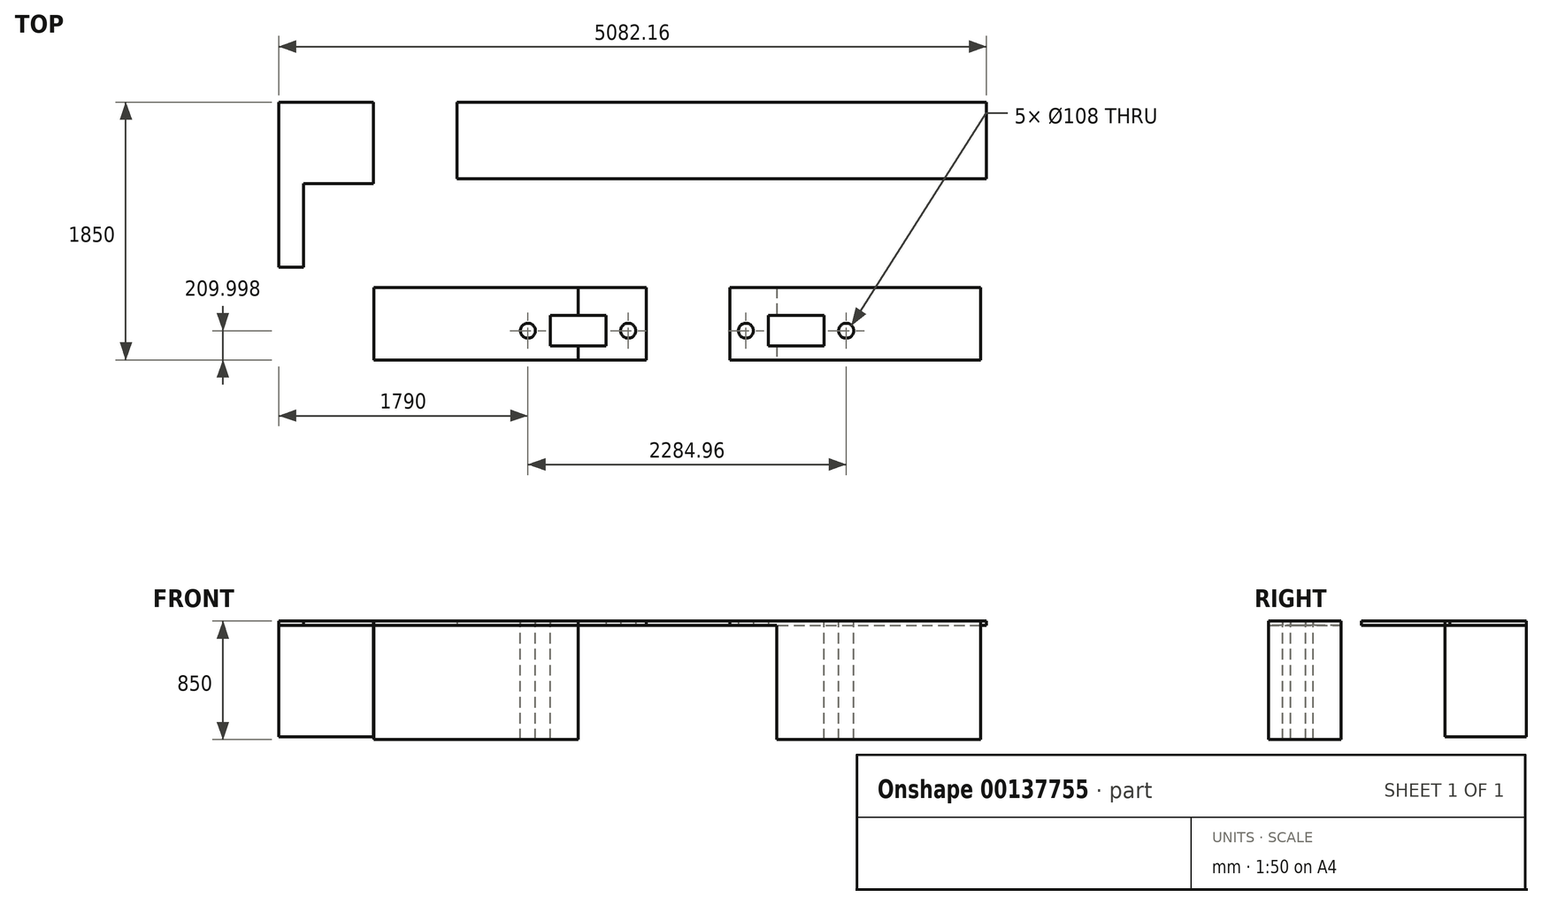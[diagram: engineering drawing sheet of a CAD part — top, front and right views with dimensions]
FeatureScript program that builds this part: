
annotation { "Feature Type Name" : "Feature", "Feature Type Description" : "" }
export const myFeature = defineFeature(function(context is Context, id is Id, definition is map)
    precondition{}
    {
        {
            var Q0;
            Q0=qCreatedBy(makeId("Top.planeOp"),FACE);
            var sketch = newSketch(context, id + "F0", { "sketchPlane" : qUnion([Q0])});
            skLineSegment(sketch, "E0", {"start": v(-2402.81, -995.48) * mm, "end": v(237.19, -995.48) * mm});
            skLineSegment(sketch, "E1", {"start": v(-2402.81, -995.48) * mm, "end": v(-2402.81, 854.52) * mm});
            skLineSegment(sketch, "E2", {"start": v(-2402.81, 854.52) * mm, "end": v(2697.19, 854.52) * mm});
            skLineSegment(sketch, "E3", {"start": v(2697.19, 854.52) * mm, "end": v(2637.19, -995.48) * mm});
            skLineSegment(sketch, "E4", {"start": v(2637.19, -995.48) * mm, "end": v(837.19, -995.48) * mm});
            skLineSegment(sketch, "E5.bottom", {"start": v(1172.19, -475.48) * mm, "end": v(2637.19, -475.48) * mm});
            skLineSegment(sketch, "E5.top", {"start": v(1172.19, -995.48) * mm, "end": v(2637.19, -995.48) * mm});
            skLineSegment(sketch, "E5.left", {"start": v(1172.19, -475.48) * mm, "end": v(1172.19, -995.48) * mm});
            skLineSegment(sketch, "E5.right", {"start": v(2637.19, -475.48) * mm, "end": v(2637.19, -995.48) * mm});
            skLineSegment(sketch, "E6.bottom", {"start": v(-2402.81, 854.52) * mm, "end": v(-1722.81, 854.52) * mm});
            skLineSegment(sketch, "E6.top", {"start": v(-2402.81, 269.52) * mm, "end": v(-1722.81, 269.52) * mm});
            skLineSegment(sketch, "E6.left", {"start": v(-2402.81, 854.52) * mm, "end": v(-2402.81, 269.52) * mm});
            skLineSegment(sketch, "E6.right", {"start": v(-1722.81, 854.52) * mm, "end": v(-1722.81, 269.52) * mm});
            skPoint(sketch, "E7", {"position": v(-252.81, -995.48) * mm});
            skLineSegment(sketch, "E8.bottom", {"start": v(-252.81, -995.48) * mm, "end": v(-1717.81, -995.48) * mm});
            skLineSegment(sketch, "E8.top", {"start": v(-252.81, -475.48) * mm, "end": v(-1717.81, -475.48) * mm});
            skLineSegment(sketch, "E8.left", {"start": v(-252.81, -995.48) * mm, "end": v(-252.81, -475.48) * mm});
            skLineSegment(sketch, "E8.right", {"start": v(-1717.81, -995.48) * mm, "end": v(-1717.81, -475.48) * mm});
            skLineSegment(sketch, "E9.bottom", {"start": v(2097.19, 854.52) * mm, "end": v(1727.19, 854.52) * mm});
            skLineSegment(sketch, "E9.top", {"start": v(2097.19, 354.52) * mm, "end": v(1727.19, 354.52) * mm});
            skLineSegment(sketch, "E9.left", {"start": v(2097.19, 854.52) * mm, "end": v(2097.19, 354.52) * mm});
            skLineSegment(sketch, "E9.right", {"start": v(1727.19, 854.52) * mm, "end": v(1727.19, 354.52) * mm});
            skLineSegment(sketch, "E10.bottom", {"start": v(1727.19, 854.52) * mm, "end": v(1397.19, 854.52) * mm});
            skLineSegment(sketch, "E10.top", {"start": v(1727.19, 534.52) * mm, "end": v(1397.19, 534.52) * mm});
            skLineSegment(sketch, "E10.left", {"start": v(1727.19, 854.52) * mm, "end": v(1727.19, 534.52) * mm});
            skLineSegment(sketch, "E10.right", {"start": v(1397.19, 854.52) * mm, "end": v(1397.19, 534.52) * mm});
            skPoint(sketch, "E11", {"position": v(-1122.81, 854.52) * mm});
            skLineSegment(sketch, "E12.bottom", {"start": v(-1122.81, 854.52) * mm, "end": v(2679.35, 854.52) * mm});
            skLineSegment(sketch, "E12.top", {"start": v(-1122.81, 304.52) * mm, "end": v(2679.35, 304.52) * mm});
            skLineSegment(sketch, "E12.left", {"start": v(-1122.81, 854.52) * mm, "end": v(-1122.81, 304.52) * mm});
            skLineSegment(sketch, "E12.right", {"start": v(2679.35, 854.52) * mm, "end": v(2679.35, 304.52) * mm});
            skLineSegment(sketch, "E13.bottom", {"start": v(237.19, -995.48) * mm, "end": v(-1722.81, -995.48) * mm});
            skLineSegment(sketch, "E13.top", {"start": v(237.19, -475.48) * mm, "end": v(-1722.81, -475.48) * mm});
            skLineSegment(sketch, "E13.left", {"start": v(237.19, -995.48) * mm, "end": v(237.19, -475.48) * mm});
            skLineSegment(sketch, "E13.right", {"start": v(-1722.81, -995.48) * mm, "end": v(-1722.81, -475.48) * mm});
            skLineSegment(sketch, "E14.bottom", {"start": v(-1722.81, 854.52) * mm, "end": v(-2402.81, 854.52) * mm});
            skLineSegment(sketch, "E14.top", {"start": v(-1722.81, -995.48) * mm, "end": v(-2402.81, -995.48) * mm});
            skLineSegment(sketch, "E14.left", {"start": v(-1722.81, 854.52) * mm, "end": v(-1722.81, -995.48) * mm});
            skLineSegment(sketch, "E14.right", {"start": v(-2402.81, 854.52) * mm, "end": v(-2402.81, -995.48) * mm});
            skLineSegment(sketch, "E15.bottom", {"start": v(837.19, -995.48) * mm, "end": v(2637.19, -995.48) * mm});
            skLineSegment(sketch, "E15.top", {"start": v(837.19, -475.48) * mm, "end": v(2637.19, -475.48) * mm});
            skLineSegment(sketch, "E15.left", {"start": v(837.19, -995.48) * mm, "end": v(837.19, -475.48) * mm});
            skLineSegment(sketch, "E15.right", {"start": v(2637.19, -995.48) * mm, "end": v(2637.19, -475.48) * mm});
            skLineSegment(sketch, "E16.bottom", {"start": v(-252.81, -995.48) * mm, "end": v(237.19, -995.48) * mm});
            skLineSegment(sketch, "E16.top", {"start": v(-252.81, -995.48) * mm, "end": v(237.19, -995.48) * mm});
            skLineSegment(sketch, "E16.left", {"start": v(-252.81, -995.48) * mm, "end": v(-252.81, -995.48) * mm});
            skLineSegment(sketch, "E16.right", {"start": v(237.19, -995.48) * mm, "end": v(237.19, -995.48) * mm});
            skLineSegment(sketch, "E17.bottom", {"start": v(-2402.81, 269.52) * mm, "end": v(-2222.81, 269.52) * mm});
            skLineSegment(sketch, "E17.top", {"start": v(-2402.81, -330.48) * mm, "end": v(-2222.81, -330.48) * mm});
            skLineSegment(sketch, "E17.left", {"start": v(-2402.81, 269.52) * mm, "end": v(-2402.81, -330.48) * mm});
            skLineSegment(sketch, "E17.right", {"start": v(-2222.81, 269.52) * mm, "end": v(-2222.81, -330.48) * mm});
            skLineSegment(sketch, "E18.bottom", {"start": v(1949.35, 854.52) * mm, "end": v(2349.35, 854.52) * mm});
            skLineSegment(sketch, "E18.top", {"start": v(1949.35, 654.52) * mm, "end": v(2349.35, 654.52) * mm});
            skLineSegment(sketch, "E18.left", {"start": v(1949.35, 854.52) * mm, "end": v(1949.35, 654.52) * mm});
            skLineSegment(sketch, "E18.right", {"start": v(2349.35, 854.52) * mm, "end": v(2349.35, 654.52) * mm});
            skCircle(sketch, "E19", {"center": v(107.19, -785.48) * mm, "radius": 54 * mm});
            skCircle(sketch, "E20", {"center": v(-612.81, -785.48) * mm, "radius": 54 * mm});
            skLineSegment(sketch, "E21.bottom", {"start": v(-452.81, -675.48) * mm, "end": v(-52.81, -675.48) * mm});
            skLineSegment(sketch, "E21.top", {"start": v(-452.81, -895.48) * mm, "end": v(-52.81, -895.48) * mm});
            skLineSegment(sketch, "E21.left", {"start": v(-452.81, -675.48) * mm, "end": v(-452.81, -895.48) * mm});
            skLineSegment(sketch, "E21.right", {"start": v(-52.81, -675.48) * mm, "end": v(-52.81, -895.48) * mm});
            skCircle(sketch, "E22", {"center": v(1672.15, -785.48) * mm, "radius": 54 * mm});
            skCircle(sketch, "E23", {"center": v(952.15, -785.48) * mm, "radius": 54 * mm});
            skLineSegment(sketch, "E24.bottom", {"start": v(1112.15, -675.48) * mm, "end": v(1512.15, -675.48) * mm});
            skLineSegment(sketch, "E24.top", {"start": v(1112.15, -895.48) * mm, "end": v(1512.15, -895.48) * mm});
            skLineSegment(sketch, "E24.left", {"start": v(1112.15, -675.48) * mm, "end": v(1112.15, -895.48) * mm});
            skLineSegment(sketch, "E24.right", {"start": v(1512.15, -675.48) * mm, "end": v(1512.15, -895.48) * mm});
            skSolve(sketch);
        }
        {
            var Q0;
            {var subQ0=sQuery(id+"F0.wireOp",EDGE,"E8.left");Q0=makeQuery(id+"F0.imprint","IMPRINT",FACE,{"disambiguationData":[TD([[makeQuery(id+"F0.imprint","IMPRINT",EDGE,{"derivedFrom":subQ0}),1.0]])]});}
            var Q1;
            {var subQ0=sQuery(id+"F0.wireOp",EDGE,"E8.top");Q1=makeQuery(id+"F0.imprint","IMPRINT",FACE,{"disambiguationData":[TD([[makeQuery(id+"F0.imprint","IMPRINT",EDGE,{"derivedFrom":subQ0}),1.0]])]});}
            extrude(context, id + "F1", {"entities" : qUnion([Q0, Q1]), "oppositeDirection" : true, "depth" : 820 * mm});
        }
        {
            var Q0;
            {var subQ4=sQuery(id+"F0.wireOp",EDGE,"E6.top");Q0=makeQuery(id+"F0.imprint","IMPRINT",FACE,{"disambiguationData":[TD([[makeQuery(id+"F0.imprint","IMPRINT",EDGE,{"derivedFrom":subQ4}),1.0]])]});}
            extrude(context, id + "F2", {"entities" : qUnion([Q0]), "oppositeDirection" : true, "depth" : 800 * mm});
        }
        {
            var Q0;
            {var subQ0=sQuery(id+"F0.wireOp",EDGE,"E5.left");Q0=makeQuery(id+"F0.imprint","IMPRINT",FACE,{"disambiguationData":[TD([[makeQuery(id+"F0.imprint","IMPRINT",EDGE,{"derivedFrom":subQ0}),1.0]])]});}
            extrude(context, id + "F3", {"entities" : qUnion([Q0]), "oppositeDirection" : true, "depth" : 820 * mm});
        }
        {
            var Q0;
            {var subQ0=sQuery(id+"F0.wireOp",EDGE,"E8.left");Q0=makeQuery(id+"F0.imprint","IMPRINT",FACE,{"disambiguationData":[TD([[makeQuery(id+"F0.imprint","IMPRINT",EDGE,{"derivedFrom":subQ0}),-1.0]])]});}
            var Q1;
            {var subQ0=sQuery(id+"F0.wireOp",EDGE,"E8.left");Q1=makeQuery(id+"F0.imprint","IMPRINT",FACE,{"disambiguationData":[TD([[makeQuery(id+"F0.imprint","IMPRINT",EDGE,{"derivedFrom":subQ0}),1.0]])]});}
            extrude(context, id + "F4", {"entities" : qUnion([Q0, Q1]), "operationType" : NewBodyOperationType.ADD, "depth" : 30 * mm});
        }
        {
            var Q0;
            {var subQ0=sQuery(id+"F0.wireOp",EDGE,"E5.left");Q0=makeQuery(id+"F0.imprint","IMPRINT",FACE,{"disambiguationData":[TD([[makeQuery(id+"F0.imprint","IMPRINT",EDGE,{"derivedFrom":subQ0}),-1.0]])]});}
            var Q1;
            {var subQ0=sQuery(id+"F0.wireOp",EDGE,"E5.left");Q1=makeQuery(id+"F0.imprint","IMPRINT",FACE,{"disambiguationData":[TD([[makeQuery(id+"F0.imprint","IMPRINT",EDGE,{"derivedFrom":subQ0}),1.0]])]});}
            extrude(context, id + "F5", {"entities" : qUnion([Q0, Q1]), "operationType" : NewBodyOperationType.ADD, "depth" : 30 * mm});
        }
        {
            var Q0;
            {var subQ5=sQuery(id+"F0.wireOp",EDGE,"E6.top");Q0=makeQuery(id+"F0.imprint","IMPRINT",FACE,{"disambiguationData":[TD([[makeQuery(id+"F0.imprint","IMPRINT",EDGE,{"derivedFrom":subQ5}),-1.0]])]});}
            var Q1;
            {var subQ0=sQuery(id+"F0.wireOp",EDGE,"E8.top");Q1=makeQuery(id+"F0.imprint","IMPRINT",FACE,{"disambiguationData":[TD([[makeQuery(id+"F0.imprint","IMPRINT",EDGE,{"derivedFrom":subQ0}),1.0]])]});}
            var Q2;
            Q2=makeQuery(id+"F0.imprint","IMPRINT",FACE,{"disambiguationData":[TD([[makeQuery(id+"F0.imprint","IMPRINT",EDGE,{"derivedFrom":sQuery(id+"F0.wireOp",EDGE,"E17.bottom")}),-1.0]])]});
            var Q3;
            {var subQ4=sQuery(id+"F0.wireOp",EDGE,"E6.top");Q3=makeQuery(id+"F0.imprint","IMPRINT",FACE,{"disambiguationData":[TD([[makeQuery(id+"F0.imprint","IMPRINT",EDGE,{"derivedFrom":subQ4}),1.0]])]});}
            extrude(context, id + "F6", {"entities" : qUnion([Q0, Q1, Q2, Q3]), "depth" : 30 * mm});
        }
        {
            var Q0;
            {var subQ5=sQuery(id+"F0.wireOp",EDGE,"E9.top");Q0=makeQuery(id+"F0.imprint","IMPRINT",FACE,{"disambiguationData":[TD([[makeQuery(id+"F0.imprint","IMPRINT",EDGE,{"derivedFrom":subQ5}),1.0]])]});}
            var Q1;
            Q1=makeQuery(id+"F0.imprint","IMPRINT",FACE,{"disambiguationData":[TD([[makeQuery(id+"F0.imprint","IMPRINT",EDGE,{"derivedFrom":sQuery(id+"F0.wireOp",EDGE,"E10.top")}),-1.0]])]});
            var Q2;
            {var subQ4=sQuery(id+"F0.wireOp",EDGE,"E9.top");Q2=makeQuery(id+"F0.imprint","IMPRINT",FACE,{"disambiguationData":[TD([[makeQuery(id+"F0.imprint","IMPRINT",EDGE,{"derivedFrom":subQ4}),-1.0]])]});}
            var Q3;
            {var subQ5=sQuery(id+"F0.wireOp",EDGE,"E18.left");Q3=makeQuery(id+"F0.imprint","IMPRINT",FACE,{"disambiguationData":[TD([[makeQuery(id+"F0.imprint","IMPRINT",EDGE,{"derivedFrom":subQ5}),1.0]])]});}
            var Q4;
            {var subQ5=sQuery(id+"F0.wireOp",EDGE,"E18.right");Q4=makeQuery(id+"F0.imprint","IMPRINT",FACE,{"disambiguationData":[TD([[makeQuery(id+"F0.imprint","IMPRINT",EDGE,{"derivedFrom":subQ5}),-1.0]])]});}
            extrude(context, id + "F7", {"entities" : qUnion([Q0, Q1, Q2, Q3, Q4]), "depth" : 30 * mm});
        }
    });
